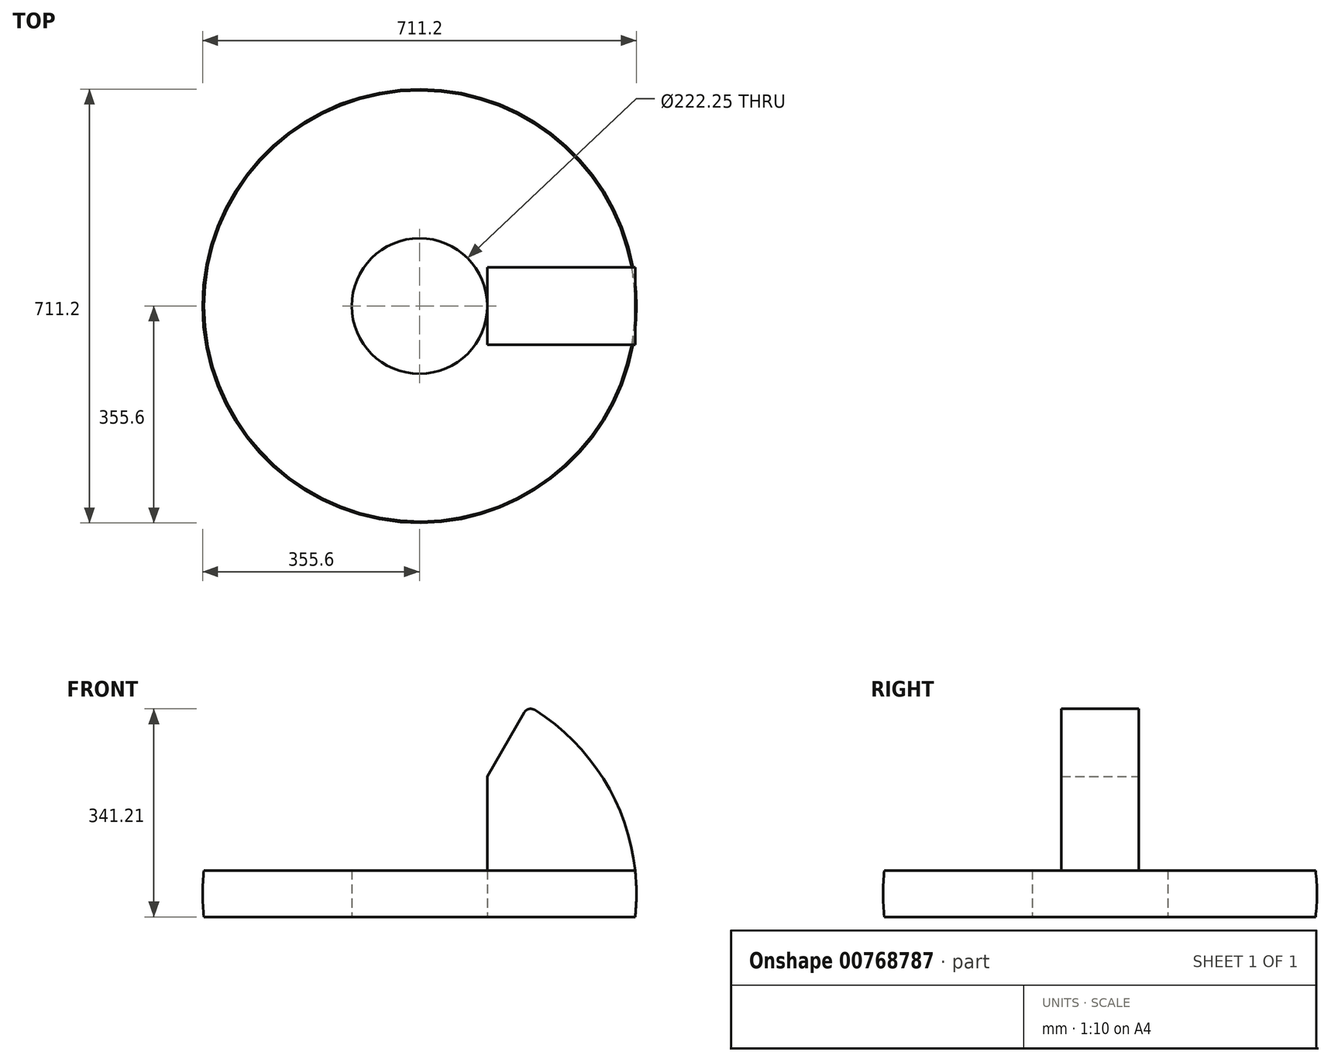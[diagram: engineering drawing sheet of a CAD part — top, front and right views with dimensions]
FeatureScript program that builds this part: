
annotation { "Feature Type Name" : "Feature", "Feature Type Description" : "" }
export const myFeature = defineFeature(function(context is Context, id is Id, definition is map)
    precondition{}
    {
        {
            var Q0;
            Q0=qCreatedBy(makeId("Front.planeOp"),FACE);
            var sketch = newSketch(context, id + "F0", { "sketchPlane" : qUnion([Q0])});
            skLineSegment(sketch, "E0", {"start": v(0, 0) * mm, "end": v(0, 1018.7) * mm, "construction": true});
            skLineSegment(sketch, "E1", {"start": v(381, 750.81) * mm, "end": v(381, -112.59) * mm, "construction": true});
            skLineSegment(sketch, "E2", {"start": v(-124.84, 645.16) * mm, "end": v(765.44, 645.16) * mm, "construction": true});
            skLineSegment(sketch, "E3", {"start": v(114.3, -53.81) * mm, "end": v(114.3, 714.98) * mm, "construction": true});
            skLineSegment(sketch, "E4", {"start": v(111.12, 342.9) * mm, "end": v(111.12, 266.7) * mm});
            skLineSegment(sketch, "E5", {"start": v(0, 304.8) * mm, "end": v(640.71, 304.8) * mm, "construction": true});
            skLineSegment(sketch, "E6", {"start": v(111.12, 342.9) * mm, "end": v(111.12, 642.78) * mm});
            skLineSegment(sketch, "E7", {"start": v(353.55, 266.7) * mm, "end": v(111.12, 266.7) * mm});
            skLineSegment(sketch, "E8", {"start": v(111.12, 342.9) * mm, "end": v(353.55, 342.9) * mm});
            skPoint(sketch, "E9.visualSharp", {"position": v(355.6, 609.6) * mm});
            skPoint(sketch, "E10.visualSharp", {"position": v(330.2, 0) * mm});
            skLineSegment(sketch, "E11.trimOffspring", {"start": v(355.6, 342.9) * mm, "end": v(355.6, 266.7) * mm, "construction": true});
            skLineSegment(sketch, "E12.trimOffspring", {"start": v(111.12, 266.7) * mm, "end": v(111.12, 112.33) * mm});
            skLineSegment(sketch, "E13", {"start": v(111.12, 497.27) * mm, "end": v(171.33, 601.56) * mm});
            skArc(sketch, "E14.trimOffspring", {"start": v(114.3, 641.72) * mm, "mid": v(112.71, 642.25) * mm, "end": v(111.12, 642.78) * mm});
            skArc(sketch, "E15", {"start": v(353.55, 342.9) * mm, "mid": v(301.52, 493.31) * mm, "end": v(189.08, 605.96) * mm});
            skArc(sketch, "E16", {"start": v(353.55, 266.7) * mm, "mid": v(355.6, 304.8) * mm, "end": v(353.55, 342.9) * mm});
            skArc(sketch, "E17.trimOffspring", {"start": v(189.08, 3.64) * mm, "mid": v(301.52, 116.29) * mm, "end": v(353.55, 266.7) * mm});
            skPoint(sketch, "E18.visualSharp", {"position": v(177.8, 612.76) * mm});
            skArc(sketch, "E18.filletArc", {"start": v(189.08, 605.96) * mm, "mid": v(179.27, 607.53) * mm, "end": v(171.33, 601.56) * mm});
            skSolve(sketch);
        }
        {
            var Q0;
            Q0=makeQuery(id+"F0.imprint","IMPRINT",FACE,{"disambiguationData":[TD([[makeQuery(id+"F0.imprint","IMPRINT",EDGE,{"derivedFrom":sQuery(id+"F0.wireOp",EDGE,"E4")}),1.0]])]});
            var Q1;
            Q1=sQuery(id+"F0.wireOp",EDGE,"E0");
            revolve(context, id + "F1", {"surfaceOperationType" : NewSurfaceOperationType.NEW, "entities" : qUnion([Q0]), "axis" : qUnion([Q1]), "revolveType" : RevolveType.FULL});
        }
        {
            var Q0;
            {var subQ1=sQuery(id+"F0.wireOp",EDGE,"E6");Q0=makeQuery(id+"F0.imprint","IMPRINT",FACE,{"disambiguationData":[TD([[makeQuery(id+"F0.imprint","IMPRINT",EDGE,{"derivedFrom":subQ1}),-1.0]])]});}
            var Q1;
            Q1=makeQuery(id+"F0.imprint","IMPRINT",FACE,{"disambiguationData":[TD([[makeQuery(id+"F0.imprint","IMPRINT",EDGE,{"derivedFrom":sQuery(id+"F0.wireOp",EDGE,"8oOEnZxF-BxU2-imYi-M3W6-jTJ36sSCfQCG")}),1.0]])]});
            extrude(context, id + "F2", {"entities" : qUnion([Q0, Q1]), "operationType" : NewBodyOperationType.ADD, "endBound" : BoundingType.SYMMETRIC, "depth" : 127 * mm, "offsetDistance" : 25.4 * mm});
        }
    });
